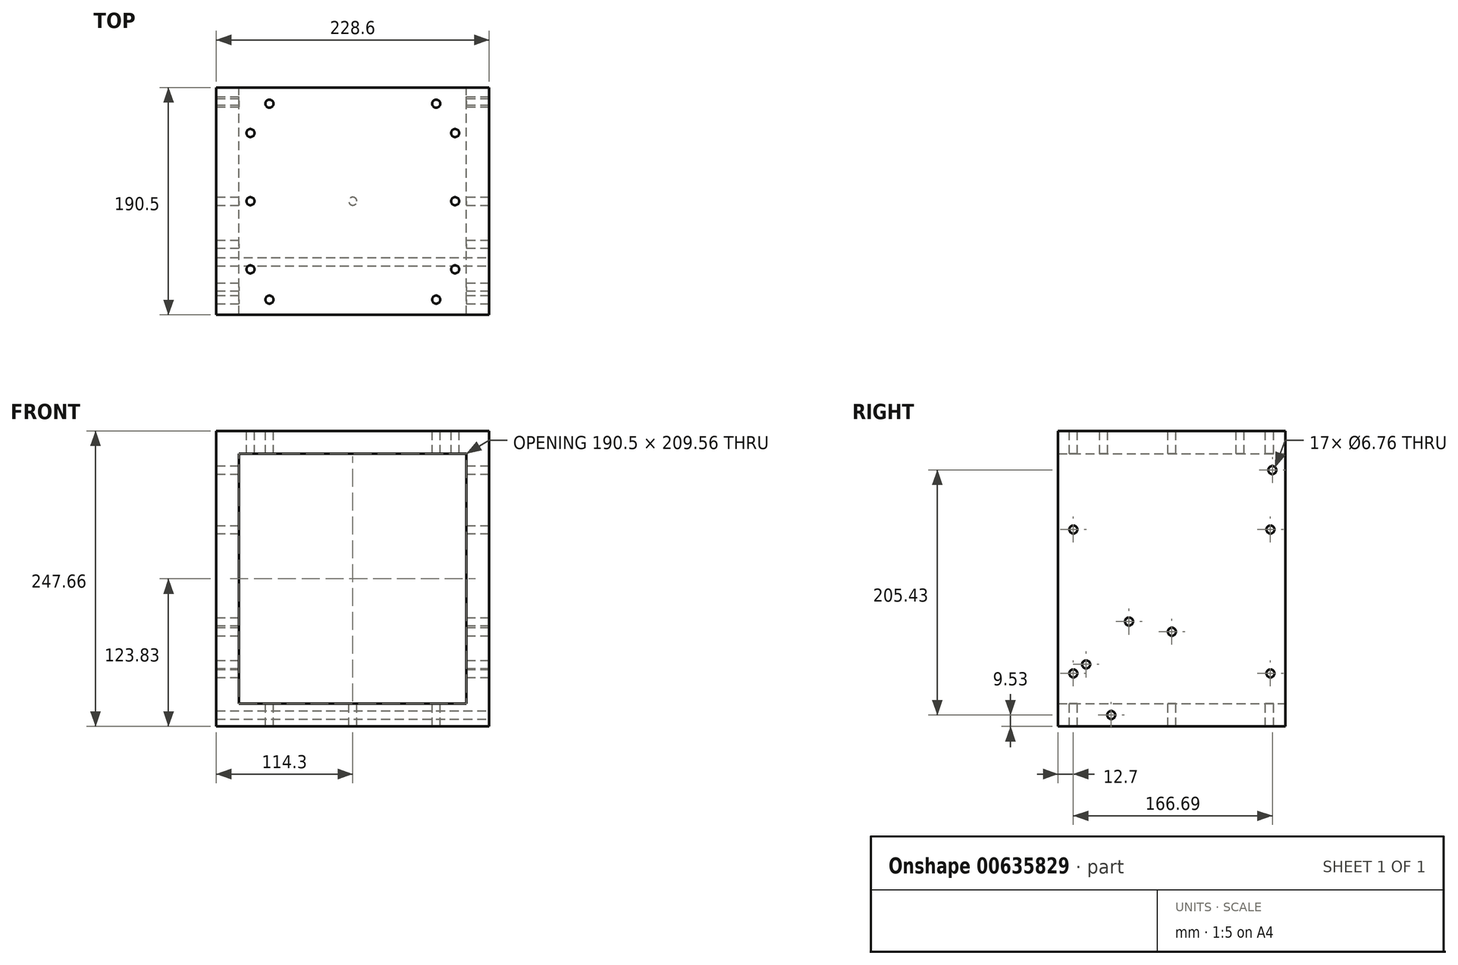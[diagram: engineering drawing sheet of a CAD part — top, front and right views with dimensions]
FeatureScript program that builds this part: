
annotation { "Feature Type Name" : "Feature", "Feature Type Description" : "" }
export const myFeature = defineFeature(function(context is Context, id is Id, definition is map)
    precondition{}
    {
        {
            var Q0;
            Q0=qCreatedBy(makeId("Front.planeOp"),FACE);
            var sketch = newSketch(context, id + "F0", { "sketchPlane" : qUnion([Q0])});
            skLineSegment(sketch, "E0.bottom", {"start": v(95.25, -104.77) * mm, "end": v(-95.25, -104.78) * mm});
            skLineSegment(sketch, "E0.top", {"start": v(95.25, 104.78) * mm, "end": v(-95.25, 104.77) * mm});
            skLineSegment(sketch, "E0.left", {"start": v(95.25, -104.77) * mm, "end": v(95.25, 104.78) * mm});
            skLineSegment(sketch, "E0.right", {"start": v(-95.25, -104.78) * mm, "end": v(-95.25, 104.77) * mm});
            skPoint(sketch, "E0.middle", {"position": v(0, 0) * mm});
            skLineSegment(sketch, "E1", {"start": v(-95.25, -104.78) * mm, "end": v(-95.25, 22.22) * mm});
            skLineSegment(sketch, "E2", {"start": v(-95.25, -104.78) * mm, "end": v(-95.25, -53.98) * mm});
            skLineSegment(sketch, "E3", {"start": v(95.25, -104.77) * mm, "end": v(95.25, -28.57) * mm});
            skLineSegment(sketch, "E4", {"start": v(-95.25, -104.78) * mm, "end": v(-44.45, -104.78) * mm});
            skLineSegment(sketch, "E5", {"start": v(95.25, -104.77) * mm, "end": v(19.05, -104.78) * mm});
            skLineSegment(sketch, "E6", {"start": v(19.05, -104.78) * mm, "end": v(95.25, -28.57) * mm});
            skLineSegment(sketch, "E7", {"start": v(-44.45, -104.78) * mm, "end": v(-95.25, -53.98) * mm});
            skLineSegment(sketch, "E8", {"start": v(-95.25, -28.58) * mm, "end": v(-95.25, 22.22) * mm});
            skLineSegment(sketch, "E9", {"start": v(95.25, -53.98) * mm, "end": v(95.25, 9.43) * mm});
            skLineSegment(sketch, "E10", {"start": v(0, 0) * mm, "end": v(0, -6.35) * mm});
            skCircle(sketch, "E11", {"center": v(0, -6.35) * mm, "radius": 79.38 * mm});
            skLineSegment(sketch, "E12.bottom", {"start": v(-95.25, 104.77) * mm, "end": v(-114.3, 104.77) * mm});
            skLineSegment(sketch, "E12.top", {"start": v(-95.25, -104.78) * mm, "end": v(-114.3, -104.78) * mm});
            skLineSegment(sketch, "E12.left", {"start": v(-95.25, 104.77) * mm, "end": v(-95.25, -104.78) * mm});
            skLineSegment(sketch, "E12.right", {"start": v(-114.3, 104.77) * mm, "end": v(-114.3, -104.78) * mm});
            skLineSegment(sketch, "E13.bottom", {"start": v(-114.3, -104.78) * mm, "end": v(114.3, -104.78) * mm});
            skLineSegment(sketch, "E13.top", {"start": v(-114.3, -123.83) * mm, "end": v(114.3, -123.83) * mm});
            skLineSegment(sketch, "E13.left", {"start": v(-114.3, -104.78) * mm, "end": v(-114.3, -123.83) * mm});
            skLineSegment(sketch, "E13.right", {"start": v(114.3, -104.78) * mm, "end": v(114.3, -123.83) * mm});
            skLineSegment(sketch, "E14.bottom", {"start": v(114.3, -104.78) * mm, "end": v(95.25, -104.78) * mm});
            skLineSegment(sketch, "E14.top", {"start": v(114.3, 104.78) * mm, "end": v(95.25, 104.78) * mm});
            skLineSegment(sketch, "E14.left", {"start": v(114.3, -104.78) * mm, "end": v(114.3, 104.77) * mm});
            skLineSegment(sketch, "E15.bottom", {"start": v(-114.3, 123.83) * mm, "end": v(114.3, 123.83) * mm});
            skLineSegment(sketch, "E15.top", {"start": v(-114.3, 104.77) * mm, "end": v(114.3, 104.77) * mm});
            skLineSegment(sketch, "E15.left", {"start": v(-114.3, 123.83) * mm, "end": v(-114.3, 104.77) * mm});
            skLineSegment(sketch, "E15.right", {"start": v(114.3, 123.83) * mm, "end": v(114.3, 104.77) * mm});
            skPoint(sketch, "E16", {"position": v(95.25, 19.05) * mm});
            skLineSegment(sketch, "E17", {"start": v(95.25, 9.43) * mm, "end": v(95.25, 95.25) * mm});
            skLineSegment(sketch, "E18", {"start": v(95.25, 95.25) * mm, "end": v(19.07, 93.44) * mm});
            skLineSegment(sketch, "E19", {"start": v(19.07, 93.44) * mm, "end": v(95.25, 19.05) * mm});
            skSolve(sketch);
        }
        {
            var Q0;
            Q0 = qSketchRegion(id + "F0", true);
            var Q1;
            Q1=makeQuery(id+"F0.imprint","IMPRINT",FACE,{"disambiguationData":[TD([[makeQuery(id+"F0.imprint","IMPRINT",EDGE,{"derivedFrom":sQuery(id+"F0.wireOp",EDGE,"E15.bottom")}),-1.0]])]});
            extrude(context, id + "F1", {"entities" : qUnion([Q0, Q1]), "depth" : 190.5 * mm, "offsetDistance" : 25.4 * mm});
        }
        {
            var Q0;
            Q0=makeQuery(id+"F1.opExtrude","SWEPT_FACE",FACE,{"disambiguationData":[OSD([sQuery(id+"F0.wireOp",EDGE,"E15.bottom")])]});
            var sketch = newSketch(context, id + "F2", { "sketchPlane" : qUnion([Q0])});
            skLineSegment(sketch, "E20", {"start": v(114.3, -190.5) * mm, "end": v(85.72, -190.5) * mm});
            skLineSegment(sketch, "E21", {"start": v(85.72, -190.5) * mm, "end": v(85.72, 0) * mm});
            skLineSegment(sketch, "E22", {"start": v(-114.3, -190.5) * mm, "end": v(-85.73, -190.5) * mm});
            skLineSegment(sketch, "E23", {"start": v(-85.73, -190.5) * mm, "end": v(-85.73, 0) * mm});
            skLineSegment(sketch, "E24", {"start": v(-85.73, 0) * mm, "end": v(-114.3, 0) * mm});
            skLineSegment(sketch, "E25", {"start": v(85.72, -190.5) * mm, "end": v(85.72, -152.4) * mm});
            skLineSegment(sketch, "E26", {"start": v(85.72, -152.4) * mm, "end": v(85.72, -95.25) * mm});
            skLineSegment(sketch, "E27", {"start": v(85.72, -95.25) * mm, "end": v(85.72, -38.1) * mm});
            skLineSegment(sketch, "E28", {"start": v(85.72, -38.1) * mm, "end": v(85.72, 0) * mm});
            skLineSegment(sketch, "E29", {"start": v(-85.73, -190.5) * mm, "end": v(-85.73, -152.4) * mm});
            skLineSegment(sketch, "E30", {"start": v(-85.73, -152.4) * mm, "end": v(-85.73, -95.25) * mm});
            skLineSegment(sketch, "E31", {"start": v(-85.73, -95.25) * mm, "end": v(-85.73, -38.1) * mm});
            skLineSegment(sketch, "E32", {"start": v(-85.73, -38.1) * mm, "end": v(-85.73, 0) * mm});
            skSolve(sketch);
        }
        {
            var Q0;
            Q0=sQuery(id+"F2.wireOp",VERTEX,"E31.end");
            var Q1;
            Q1=sQuery(id+"F2.wireOp",VERTEX,"E30.end");
            var Q2;
            Q2=sQuery(id+"F2.wireOp",VERTEX,"E29.end");
            var Q3;
            Q3=sQuery(id+"F2.wireOp",VERTEX,"E26.start");
            var Q4;
            Q4=sQuery(id+"F2.wireOp",VERTEX,"E27.start");
            var Q5;
            Q5=sQuery(id+"F2.wireOp",VERTEX,"E28.start");
            var Q6;
            Q6=makeQuery(id+"F1.opExtrude","SWEPT_BODY",BODY,{"disambiguationData":[OSD([sQuery(id+"F0.wireOp",EDGE,"E12.left"),sQuery(id+"F0.wireOp",EDGE,"E12.right"),sQuery(id+"F0.wireOp",EDGE,"E13.bottom"),sQuery(id+"F0.wireOp",EDGE,"E13.top"),sQuery(id+"F0.wireOp",EDGE,"E13.left"),sQuery(id+"F0.wireOp",EDGE,"E13.right"),sQuery(id+"F0.wireOp",EDGE,"E14.left"),sQuery(id+"F0.wireOp",EDGE,"E0.left"),sQuery(id+"F0.wireOp",EDGE,"E15.bottom"),sQuery(id+"F0.wireOp",EDGE,"E15.top"),sQuery(id+"F0.wireOp",EDGE,"E15.left"),sQuery(id+"F0.wireOp",EDGE,"E15.right")])]});
            hole(context, id + "F3", {"style" : HoleStyle.SIMPLE, "endStyle" : HoleEndStyle.BLIND, "standardTappedOrClearance" : lookupTablePath({ "standard" : "ANSI", "fit" : "Normal (ASME)", "size" : "1/4", "type" : "Clearance" }), "standardBlindInLast" : lookupTablePath({ "fit" : "Free", "standard" : "ANSI", "size" : "1/4", "type" : "Clearance" }), "holeDiameter" : 6.76 * mm, "majorDiameter" : 6.35 * mm, "holeDepth" : 50.8 * mm, "isTappedThrough" : true, "tappedDepth" : 12.7 * mm, "tapClearance" : 3, "locations" : qUnion([Q0, Q1, Q2, Q3, Q4, Q5]), "scope" : qUnion([Q6])});
        }
        {
            var Q0;
            Q0=makeQuery(id+"F1.opExtrude","SWEPT_FACE",FACE,{"disambiguationData":[OSD([sQuery(id+"F0.wireOp",EDGE,"E15.bottom")])]});
            var sketch = newSketch(context, id + "F4", { "sketchPlane" : qUnion([Q0])});
            skLineSegment(sketch, "E33", {"start": v(-114.3, 0) * mm, "end": v(-69.85, 0) * mm});
            skLineSegment(sketch, "E34", {"start": v(-69.85, 0) * mm, "end": v(-69.85, -13.47) * mm});
            skLineSegment(sketch, "E35", {"start": v(-69.85, -13.47) * mm, "end": v(69.85, -13.47) * mm});
            skLineSegment(sketch, "E36", {"start": v(69.85, -13.47) * mm, "end": v(69.85, -177.8) * mm});
            skLineSegment(sketch, "E37", {"start": v(69.85, -177.8) * mm, "end": v(-69.85, -177.8) * mm});
            skLineSegment(sketch, "E38", {"start": v(-69.85, -177.8) * mm, "end": v(-69.85, -13.47) * mm});
            skSolve(sketch);
        }
        {
            var Q0;
            Q0=sQuery(id+"F4.wireOp",VERTEX,"E38.end");
            var Q1;
            Q1=sQuery(id+"F4.wireOp",VERTEX,"E36.start");
            var Q2;
            Q2=sQuery(id+"F4.wireOp",VERTEX,"E37.start");
            var Q3;
            Q3=sQuery(id+"F4.wireOp",VERTEX,"E38.start");
            var Q4;
            Q4=makeQuery(id+"F1.opExtrude","SWEPT_BODY",BODY,{"disambiguationData":[OSD([sQuery(id+"F0.wireOp",EDGE,"E12.left"),sQuery(id+"F0.wireOp",EDGE,"E12.right"),sQuery(id+"F0.wireOp",EDGE,"E13.bottom"),sQuery(id+"F0.wireOp",EDGE,"E13.top"),sQuery(id+"F0.wireOp",EDGE,"E13.left"),sQuery(id+"F0.wireOp",EDGE,"E13.right"),sQuery(id+"F0.wireOp",EDGE,"E14.left"),sQuery(id+"F0.wireOp",EDGE,"E0.left"),sQuery(id+"F0.wireOp",EDGE,"E15.bottom"),sQuery(id+"F0.wireOp",EDGE,"E15.top"),sQuery(id+"F0.wireOp",EDGE,"E15.left"),sQuery(id+"F0.wireOp",EDGE,"E15.right")])]});
            hole(context, id + "F5", {"style" : HoleStyle.SIMPLE, "endStyle" : HoleEndStyle.THROUGH, "standardTappedOrClearance" : lookupTablePath({ "standard" : "ANSI", "fit" : "Normal (ASME)", "size" : "1/4", "type" : "Clearance" }), "standardBlindInLast" : lookupTablePath({ "fit" : "Free", "standard" : "ANSI", "size" : "1/4", "type" : "Clearance" }), "holeDiameter" : 6.76 * mm, "majorDiameter" : 6.35 * mm, "isTappedThrough" : true, "tappedDepth" : 12.7 * mm, "tapClearance" : 3, "locations" : qUnion([Q0, Q1, Q2, Q3]), "scope" : qUnion([Q4])});
        }
        {
            var Q0;
            Q0=makeQuery(id+"F1.opExtrude","SWEPT_FACE",FACE,{"disambiguationData":[OSD([sQuery(id+"F0.wireOp",EDGE,"E13.right"),sQuery(id+"F0.wireOp",EDGE,"E14.left"),sQuery(id+"F0.wireOp",EDGE,"E15.right")])]});
            var sketch = newSketch(context, id + "F6", { "sketchPlane" : qUnion([Q0])});
            skLineSegment(sketch, "E39", {"start": v(-190.5, -123.83) * mm, "end": v(-177.8, -123.83) * mm});
            skLineSegment(sketch, "E40", {"start": v(-177.8, -123.83) * mm, "end": v(-177.8, -79.38) * mm});
            skLineSegment(sketch, "E41", {"start": v(-177.8, -79.38) * mm, "end": v(-177.8, 41.27) * mm});
            skLineSegment(sketch, "E42", {"start": v(-177.8, 41.27) * mm, "end": v(-12.7, 41.27) * mm});
            skLineSegment(sketch, "E43", {"start": v(-12.7, 41.27) * mm, "end": v(-12.7, -79.38) * mm});
            skLineSegment(sketch, "E44", {"start": v(-12.7, -79.38) * mm, "end": v(-177.8, -79.38) * mm});
            skSolve(sketch);
        }
        {
            var Q0;
            Q0=sQuery(id+"F6.wireOp",VERTEX,"E42.start");
            var Q1;
            Q1=sQuery(id+"F6.wireOp",VERTEX,"E43.start");
            var Q2;
            Q2=sQuery(id+"F6.wireOp",VERTEX,"E43.end");
            var Q3;
            Q3=sQuery(id+"F6.wireOp",VERTEX,"E44.end");
            var Q4;
            Q4=makeQuery(id+"F1.opExtrude","SWEPT_BODY",BODY,{"disambiguationData":[OSD([sQuery(id+"F0.wireOp",EDGE,"E12.left"),sQuery(id+"F0.wireOp",EDGE,"E12.right"),sQuery(id+"F0.wireOp",EDGE,"E13.bottom"),sQuery(id+"F0.wireOp",EDGE,"E13.top"),sQuery(id+"F0.wireOp",EDGE,"E13.left"),sQuery(id+"F0.wireOp",EDGE,"E13.right"),sQuery(id+"F0.wireOp",EDGE,"E14.left"),sQuery(id+"F0.wireOp",EDGE,"E0.left"),sQuery(id+"F0.wireOp",EDGE,"E15.bottom"),sQuery(id+"F0.wireOp",EDGE,"E15.top"),sQuery(id+"F0.wireOp",EDGE,"E15.left"),sQuery(id+"F0.wireOp",EDGE,"E15.right")])]});
            hole(context, id + "F7", {"style" : HoleStyle.SIMPLE, "endStyle" : HoleEndStyle.THROUGH, "standardTappedOrClearance" : lookupTablePath({ "standard" : "ANSI", "fit" : "Normal (ASME)", "size" : "1/4", "type" : "Clearance" }), "standardBlindInLast" : lookupTablePath({ "fit" : "Free", "standard" : "ANSI", "size" : "1/4", "type" : "Clearance" }), "holeDiameter" : 6.76 * mm, "majorDiameter" : 6.35 * mm, "isTappedThrough" : true, "tappedDepth" : 12.7 * mm, "tapClearance" : 3, "locations" : qUnion([Q0, Q1, Q2, Q3]), "scope" : qUnion([Q4])});
        }
        {
            var Q0;
            Q0=makeQuery(id+"F1.opExtrude","SWEPT_FACE",FACE,{"disambiguationData":[OSD([sQuery(id+"F0.wireOp",EDGE,"E13.right"),sQuery(id+"F0.wireOp",EDGE,"E14.left"),sQuery(id+"F0.wireOp",EDGE,"E15.right")])]});
            var sketch = newSketch(context, id + "F8", { "sketchPlane" : qUnion([Q0])});
            skLineSegment(sketch, "E45", {"start": v(-190.5, -123.83) * mm, "end": v(-95.25, -123.83) * mm});
            skLineSegment(sketch, "E46", {"start": v(-95.25, -123.83) * mm, "end": v(-95.25, -44.45) * mm});
            skSolve(sketch);
        }
        {
            var Q0;
            Q0=sQuery(id+"F8.wireOp",VERTEX,"E46.end");
            var Q1;
            Q1=makeQuery(id+"F1.opExtrude","SWEPT_BODY",BODY,{"disambiguationData":[OSD([sQuery(id+"F0.wireOp",EDGE,"E12.left"),sQuery(id+"F0.wireOp",EDGE,"E12.right"),sQuery(id+"F0.wireOp",EDGE,"E13.bottom"),sQuery(id+"F0.wireOp",EDGE,"E13.top"),sQuery(id+"F0.wireOp",EDGE,"E13.left"),sQuery(id+"F0.wireOp",EDGE,"E13.right"),sQuery(id+"F0.wireOp",EDGE,"E14.left"),sQuery(id+"F0.wireOp",EDGE,"E0.left"),sQuery(id+"F0.wireOp",EDGE,"E15.bottom"),sQuery(id+"F0.wireOp",EDGE,"E15.top"),sQuery(id+"F0.wireOp",EDGE,"E15.left"),sQuery(id+"F0.wireOp",EDGE,"E15.right")])]});
            hole(context, id + "F9", {"style" : HoleStyle.SIMPLE, "endStyle" : HoleEndStyle.THROUGH, "standardTappedOrClearance" : lookupTablePath({ "standard" : "ANSI", "fit" : "Normal (ASME)", "size" : "1/4", "type" : "Clearance" }), "standardBlindInLast" : lookupTablePath({ "fit" : "Free", "standard" : "ANSI", "size" : "1/4", "type" : "Clearance" }), "holeDiameter" : 6.76 * mm, "majorDiameter" : 6.35 * mm, "isTappedThrough" : true, "tappedDepth" : 12.7 * mm, "tapClearance" : 3, "locations" : qUnion([Q0]), "scope" : qUnion([Q1])});
        }
        {
            var Q0;
            Q0=makeQuery(id+"F1.opExtrude","SWEPT_FACE",FACE,{"disambiguationData":[OSD([sQuery(id+"F0.wireOp",EDGE,"E13.bottom")])]});
            var sketch = newSketch(context, id + "F10", { "sketchPlane" : qUnion([Q0])});
            skLineSegment(sketch, "E47", {"start": v(95.25, 0) * mm, "end": v(-95.25, 0) * mm});
            skLineSegment(sketch, "E48", {"start": v(-95.25, 0) * mm, "end": v(0, 0) * mm});
            skLineSegment(sketch, "E49", {"start": v(0, 0) * mm, "end": v(0, -190.5) * mm});
            skLineSegment(sketch, "E50", {"start": v(0, -190.5) * mm, "end": v(0, -95.25) * mm});
            skSolve(sketch);
        }
        {
            var Q0;
            Q0=sQuery(id+"F10.wireOp",VERTEX,"E50.end");
            var Q1;
            Q1=makeQuery(id+"F1.opExtrude","SWEPT_BODY",BODY,{"disambiguationData":[OSD([sQuery(id+"F0.wireOp",EDGE,"E12.left"),sQuery(id+"F0.wireOp",EDGE,"E12.right"),sQuery(id+"F0.wireOp",EDGE,"E13.bottom"),sQuery(id+"F0.wireOp",EDGE,"E13.top"),sQuery(id+"F0.wireOp",EDGE,"E13.left"),sQuery(id+"F0.wireOp",EDGE,"E13.right"),sQuery(id+"F0.wireOp",EDGE,"E14.left"),sQuery(id+"F0.wireOp",EDGE,"E0.left"),sQuery(id+"F0.wireOp",EDGE,"E15.bottom"),sQuery(id+"F0.wireOp",EDGE,"E15.top"),sQuery(id+"F0.wireOp",EDGE,"E15.left"),sQuery(id+"F0.wireOp",EDGE,"E15.right")])]});
            hole(context, id + "F11", {"style" : HoleStyle.SIMPLE, "endStyle" : HoleEndStyle.THROUGH, "standardTappedOrClearance" : lookupTablePath({ "standard" : "ANSI", "fit" : "Normal (ASME)", "size" : "1/4", "type" : "Clearance" }), "standardBlindInLast" : lookupTablePath({ "fit" : "Free", "standard" : "ANSI", "size" : "1/4", "type" : "Clearance" }), "holeDiameter" : 6.76 * mm, "majorDiameter" : 6.35 * mm, "isTappedThrough" : true, "tappedDepth" : 12.7 * mm, "tapClearance" : 3, "locations" : qUnion([Q0]), "scope" : qUnion([Q1])});
        }
        {
            var Q0;
            Q0=makeQuery(id+"F1.opExtrude","SWEPT_FACE",FACE,{"disambiguationData":[OSD([sQuery(id+"F0.wireOp",EDGE,"E13.right"),sQuery(id+"F0.wireOp",EDGE,"E14.left"),sQuery(id+"F0.wireOp",EDGE,"E15.right")])]});
            var sketch = newSketch(context, id + "F12", { "sketchPlane" : qUnion([Q0])});
            skLineSegment(sketch, "E51", {"start": v(-190.5, -123.83) * mm, "end": v(-190.5, -104.78) * mm});
            skLineSegment(sketch, "E52", {"start": v(-190.5, -104.78) * mm, "end": v(-155.58, -104.78) * mm});
            skLineSegment(sketch, "E53", {"start": v(-155.58, -104.78) * mm, "end": v(-22.22, 98.43) * mm});
            skLineSegment(sketch, "E54", {"start": v(-22.23, 98.42) * mm, "end": v(0, 98.42) * mm});
            skLineSegment(sketch, "E55", {"start": v(0, 98.42) * mm, "end": v(0, 123.83) * mm});
            skLineSegment(sketch, "E56", {"start": v(-155.58, -104.78) * mm, "end": v(-174.63, -123.83) * mm});
            skLineSegment(sketch, "E57", {"start": v(-174.63, -123.83) * mm, "end": v(-165.1, -114.3) * mm});
            skLineSegment(sketch, "E58", {"start": v(-155.58, -104.78) * mm, "end": v(-136.53, -123.83) * mm});
            skLineSegment(sketch, "E59", {"start": v(-136.53, -123.83) * mm, "end": v(-146.05, -114.3) * mm});
            skLineSegment(sketch, "E60", {"start": v(-22.23, 98.42) * mm, "end": v(0, 83.84) * mm});
            skLineSegment(sketch, "E61", {"start": v(0, 83.84) * mm, "end": v(-11.11, 91.13) * mm});
            skLineSegment(sketch, "E62", {"start": v(-95.25, -123.83) * mm, "end": v(-95.25, 0) * mm});
            skCircle(sketch, "E63", {"center": v(-95.25, 0) * mm, "radius": 50.8 * mm});
            skCircle(sketch, "E64", {"center": v(-95.25, 0) * mm, "radius": 101.6 * mm});
            skPoint(sketch, "E65", {"position": v(-116.96, -45.93) * mm});
            skPoint(sketch, "E66", {"position": v(-144.96, -88.6) * mm});
            skLineSegment(sketch, "E67", {"start": v(-95.25, 0) * mm, "end": v(-146.05, 0) * mm});
            skLineSegment(sketch, "E68", {"start": v(-146.05, 0) * mm, "end": v(-95.25, -50.8) * mm});
            skLineSegment(sketch, "E69", {"start": v(-95.25, 0) * mm, "end": v(-120.65, -25.4) * mm});
            skLineSegment(sketch, "E70", {"start": v(-120.65, -25.4) * mm, "end": v(-167.1, -71.84) * mm});
            skPoint(sketch, "E71", {"position": v(-131.17, -35.92) * mm});
            skSolve(sketch);
        }
        {
            var Q0;
            Q0=sQuery(id+"F12.wireOp",VERTEX,"E59.end");
            var Q1;
            Q1=sQuery(id+"F12.wireOp",VERTEX,"E61.end");
            var Q2;
            Q2=sQuery(id+"F12.wireOp",VERTEX,"E71");
            var Q3;
            Q3=sQuery(id+"F12.wireOp",VERTEX,"E70.end");
            var Q4;
            Q4=makeQuery(id+"F1.opExtrude","SWEPT_BODY",BODY,{"disambiguationData":[OSD([sQuery(id+"F0.wireOp",EDGE,"E12.left"),sQuery(id+"F0.wireOp",EDGE,"E12.right"),sQuery(id+"F0.wireOp",EDGE,"E13.bottom"),sQuery(id+"F0.wireOp",EDGE,"E13.top"),sQuery(id+"F0.wireOp",EDGE,"E13.left"),sQuery(id+"F0.wireOp",EDGE,"E13.right"),sQuery(id+"F0.wireOp",EDGE,"E14.left"),sQuery(id+"F0.wireOp",EDGE,"E0.left"),sQuery(id+"F0.wireOp",EDGE,"E15.bottom"),sQuery(id+"F0.wireOp",EDGE,"E15.top"),sQuery(id+"F0.wireOp",EDGE,"E15.left"),sQuery(id+"F0.wireOp",EDGE,"E15.right")])]});
            hole(context, id + "F13", {"style" : HoleStyle.SIMPLE, "endStyle" : HoleEndStyle.THROUGH, "standardTappedOrClearance" : lookupTablePath({ "standard" : "ANSI", "fit" : "Normal (ASME)", "size" : "1/4", "type" : "Clearance" }), "standardBlindInLast" : lookupTablePath({ "fit" : "Free", "standard" : "ANSI", "size" : "1/4", "type" : "Clearance" }), "holeDiameter" : 6.76 * mm, "majorDiameter" : 6.35 * mm, "isTappedThrough" : true, "tappedDepth" : 12.7 * mm, "tapClearance" : 3, "locations" : qUnion([Q0, Q1, Q2, Q3]), "scope" : qUnion([Q4])});
        }
    });
